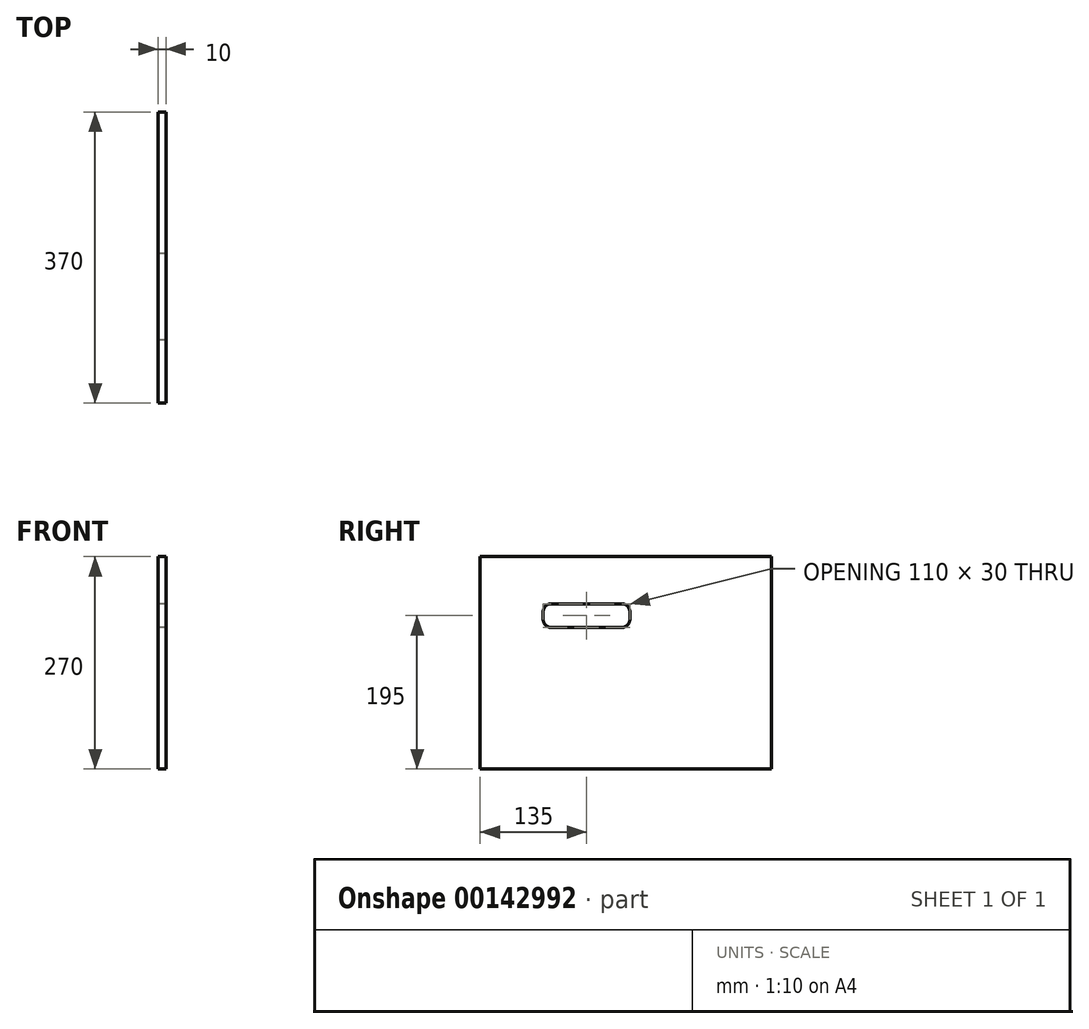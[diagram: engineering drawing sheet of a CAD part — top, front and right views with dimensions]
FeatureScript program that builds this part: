
annotation { "Feature Type Name" : "Feature", "Feature Type Description" : "" }
export const myFeature = defineFeature(function(context is Context, id is Id, definition is map)
    precondition{}
    {
        {
            var Q0;
            Q0=qCreatedBy(makeId("Right.planeOp"),FACE);
            var sketch = newSketch(context, id + "F0", { "sketchPlane" : qUnion([Q0])});
            skLineSegment(sketch, "E0.bottom", {"start": v(0, 0) * mm, "end": v(370, 0) * mm});
            skLineSegment(sketch, "E0.top", {"start": v(0, 270) * mm, "end": v(370, 270) * mm});
            skLineSegment(sketch, "E0.left", {"start": v(0, 0) * mm, "end": v(0, 270) * mm});
            skLineSegment(sketch, "E0.right", {"start": v(370, 0) * mm, "end": v(370, 270) * mm});
            skLineSegment(sketch, "E1", {"start": v(0, 210) * mm, "end": v(370, 210) * mm, "construction": true});
            skLineSegment(sketch, "E2.bottom", {"start": v(90, 210) * mm, "end": v(180, 210) * mm});
            skLineSegment(sketch, "E2.top", {"start": v(90, 180) * mm, "end": v(180, 180) * mm});
            skLineSegment(sketch, "E2.left", {"start": v(80, 200) * mm, "end": v(80, 190) * mm});
            skLineSegment(sketch, "E2.right", {"start": v(190, 200) * mm, "end": v(190, 190) * mm});
            skPoint(sketch, "E3", {"position": v(169.51, 210) * mm});
            skPoint(sketch, "E4.visualSharp", {"position": v(190, 210) * mm});
            skArc(sketch, "E4.filletArc", {"start": v(190, 200) * mm, "mid": v(187.07, 207.07) * mm, "end": v(180, 210) * mm});
            skPoint(sketch, "E5.visualSharp", {"position": v(190, 180) * mm});
            skArc(sketch, "E5.filletArc", {"start": v(180, 180) * mm, "mid": v(187.07, 182.93) * mm, "end": v(190, 190) * mm});
            skPoint(sketch, "E6.visualSharp", {"position": v(80, 210) * mm});
            skArc(sketch, "E6.filletArc", {"start": v(90, 210) * mm, "mid": v(82.93, 207.07) * mm, "end": v(80, 200) * mm});
            skPoint(sketch, "E7.visualSharp", {"position": v(80, 180) * mm});
            skArc(sketch, "E7.filletArc", {"start": v(80, 190) * mm, "mid": v(82.93, 182.93) * mm, "end": v(90, 180) * mm});
            skPoint(sketch, "E8", {"position": v(135, 210) * mm});
            skSolve(sketch);
        }
        {
            var Q0;
            Q0 = qSketchRegion(id + "F0", true);
            extrude(context, id + "F1", {"entities" : qUnion([Q0]), "depth" : 10 * mm, "offsetDistance" : 25 * mm});
        }
    });
